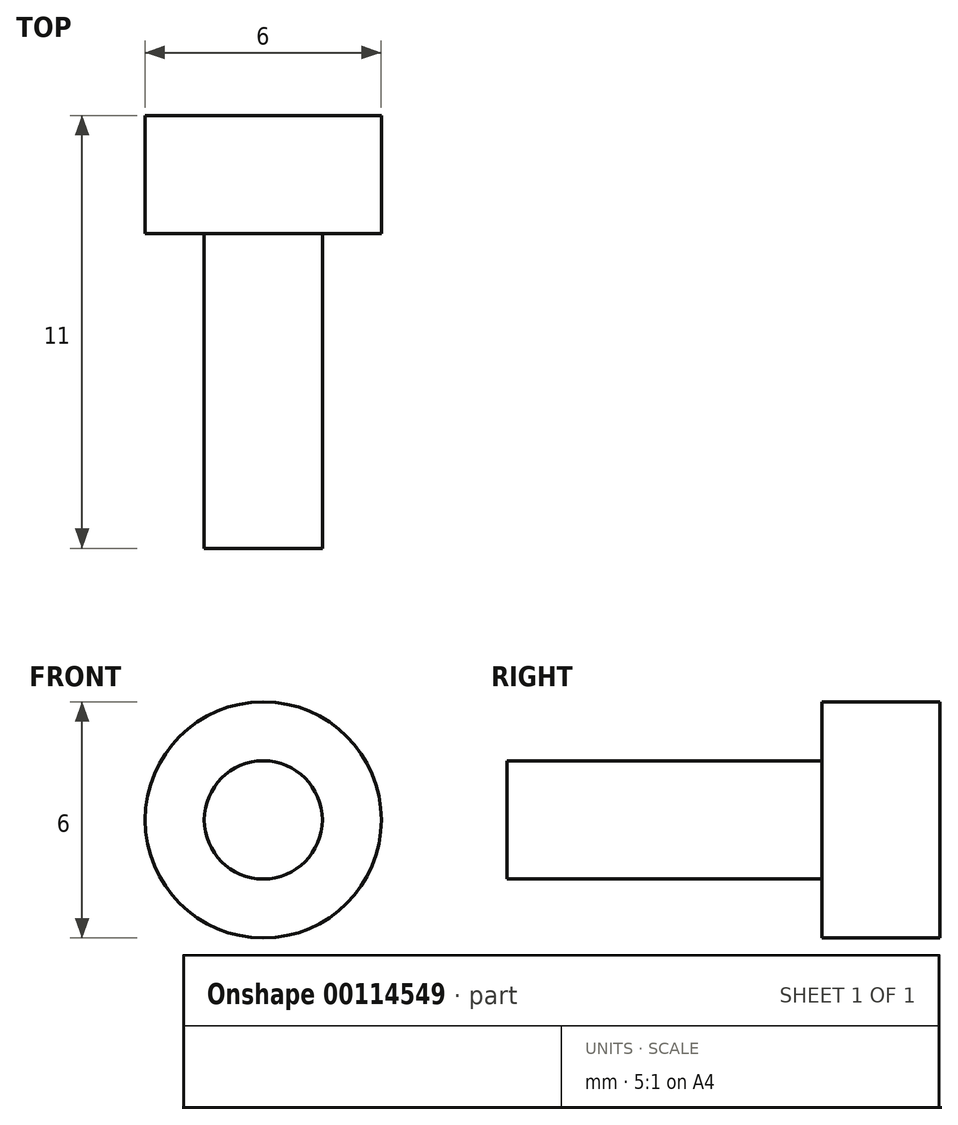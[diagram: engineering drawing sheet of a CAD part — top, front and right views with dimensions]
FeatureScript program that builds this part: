
annotation { "Feature Type Name" : "Feature", "Feature Type Description" : "" }
export const myFeature = defineFeature(function(context is Context, id is Id, definition is map)
    precondition{}
    {
        {
            var Q0;
            Q0=qCreatedBy(makeId("Front.planeOp"),FACE);
            var sketch = newSketch(context, id + "F0", { "sketchPlane" : qUnion([Q0])});
            skCircle(sketch, "E0", {"center": v(-47.62, 6.96) * mm, "radius": 3 * mm});
            skSolve(sketch);
        }
        {
            var Q0;
            Q0=qSketchRegion(id+"F0",true);
            extrude(context, id + "F1", {"entities" : qUnion([Q0]), "depth" : 3 * mm});
        }
        {
            var Q0;
            Q0=makeQuery(id+"F1.opExtrude","CAP_FACE",FACE,{"disambiguationData":[OSD([sQuery(id+"F0.wireOp",EDGE,"E0")])],"isStart":false});
            var sketch = newSketch(context, id + "F2", { "sketchPlane" : qUnion([Q0])});
            skLineSegment(sketch, "E1", {"start": v(-47.62, 9.96) * mm, "end": v(-47.62, 3.96) * mm, "construction": true});
            skCircle(sketch, "E2", {"center": v(-47.62, 6.96) * mm, "radius": 1.5 * mm});
            skSolve(sketch);
        }
        {
            var Q0;
            Q0=qSketchRegion(id+"F2",true);
            extrude(context, id + "F3", {"entities" : qUnion([Q0]), "operationType" : NewBodyOperationType.ADD, "depth" : 8 * mm});
        }
    });
